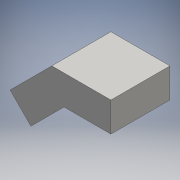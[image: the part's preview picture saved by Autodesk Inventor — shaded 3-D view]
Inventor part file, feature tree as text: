
AUTODESK INVENTOR PART (.ipt)
format: ipt  version: 2016 (Build 200138000, 138)  size: 93,184 bytes
history: native  units: mm
features: extrude x1, sketch x1
ambient origin geometry x8: Origin, YZ Plane, XZ Plane, XY Plane, X Axis, Y Axis, Z Axis, Center Point
bodies: Solid1 (feature_tree)
feature tree (2):
  extrude  "Extrusion1"  Depth=10.0mm
  sketch  "Sketch1"  dims[d0=20.0mm d6=10.0mm d10=45.0deg d11=20.0mm d12=0.0mm]
